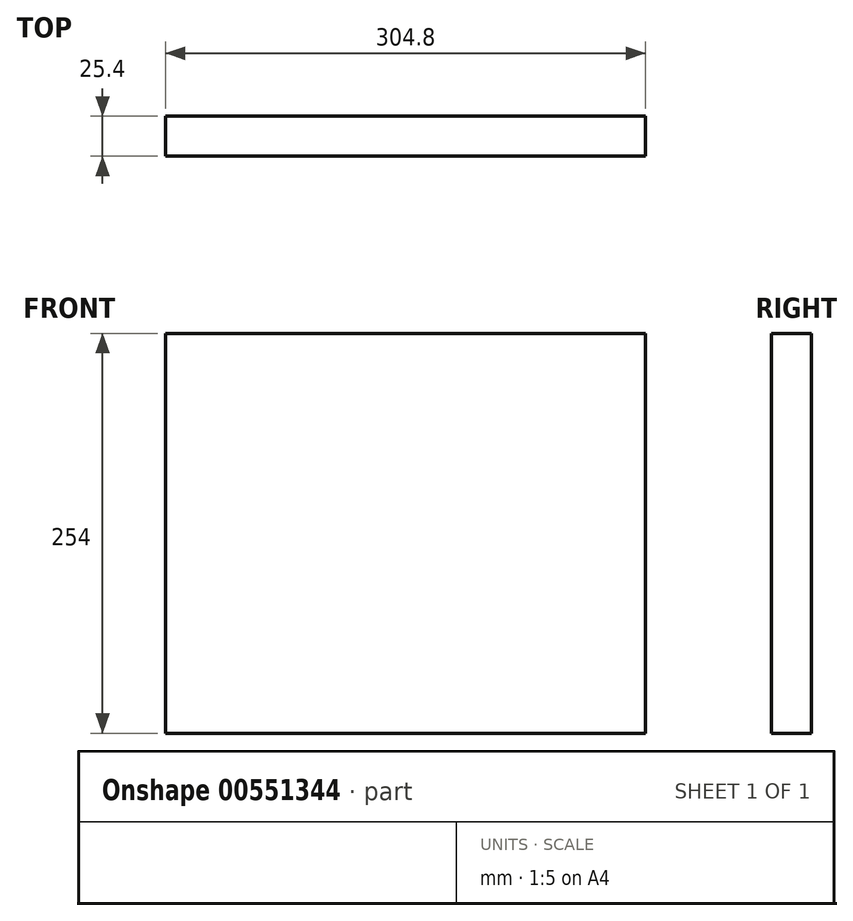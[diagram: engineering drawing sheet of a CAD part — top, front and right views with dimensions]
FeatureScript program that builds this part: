
annotation { "Feature Type Name" : "Feature", "Feature Type Description" : "" }
export const myFeature = defineFeature(function(context is Context, id is Id, definition is map)
    precondition{}
    {
        {
            var Q0;
            Q0=qCreatedBy(makeId("Front.planeOp"),FACE);
            var sketch = newSketch(context, id + "F0", { "sketchPlane" : qUnion([Q0])});
            skLineSegment(sketch, "E0.bottom", {"start": v(-153.2, 134.77) * mm, "end": v(151.6, 134.77) * mm});
            skLineSegment(sketch, "E0.top", {"start": v(-153.2, -119.23) * mm, "end": v(151.6, -119.23) * mm});
            skLineSegment(sketch, "E0.left", {"start": v(-153.2, 134.77) * mm, "end": v(-153.2, -119.23) * mm});
            skLineSegment(sketch, "E0.right", {"start": v(151.6, 134.77) * mm, "end": v(151.6, -119.23) * mm});
            skSolve(sketch);
        }
        {
            var Q0;
            Q0 = qSketchRegion(id + "F0", true);
            extrude(context, id + "F1", {"entities" : qUnion([Q0]), "depth" : 25.4 * mm, "offsetDistance" : 25.4 * mm});
        }
    });
